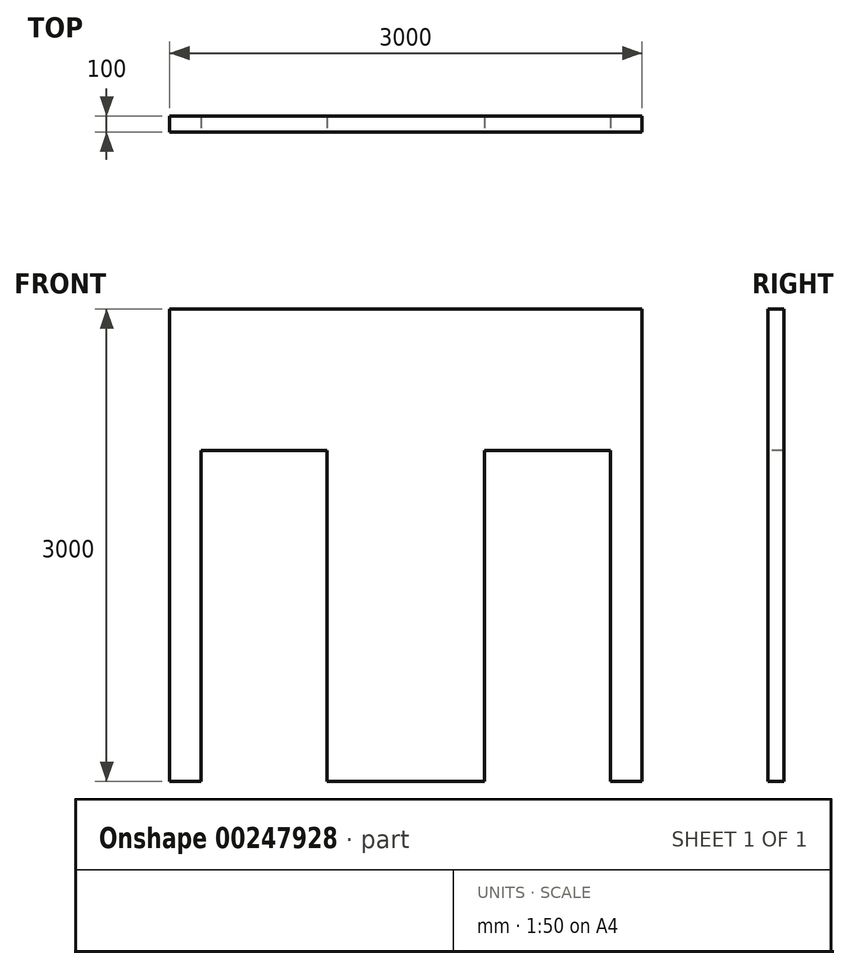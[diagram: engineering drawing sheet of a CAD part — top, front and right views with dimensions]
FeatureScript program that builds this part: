
annotation { "Feature Type Name" : "Feature", "Feature Type Description" : "" }
export const myFeature = defineFeature(function(context is Context, id is Id, definition is map)
    precondition{}
    {
        {
            var Q0;
            Q0=qCreatedBy(makeId("Front.planeOp"),FACE);
            var sketch = newSketch(context, id + "F0", { "sketchPlane" : qUnion([Q0])});
            skLineSegment(sketch, "E0.bottom", {"start": v(1500, 0) * mm, "end": v(-1500, 0) * mm});
            skLineSegment(sketch, "E0.top", {"start": v(1500, 3000) * mm, "end": v(-1500, 3000) * mm});
            skLineSegment(sketch, "E0.left", {"start": v(1500, 0) * mm, "end": v(1500, 3000) * mm});
            skLineSegment(sketch, "E0.right", {"start": v(-1500, 0) * mm, "end": v(-1500, 3000) * mm});
            skPoint(sketch, "E0.middle", {"position": v(0, 1500) * mm});
            skSolve(sketch);
        }
        {
            var Q0;
            Q0=makeQuery(id+"F0.imprint","IMPRINT",FACE,{"disambiguationData":[TD([[makeQuery(id+"F0.imprint","IMPRINT",EDGE,{"derivedFrom":sQuery(id+"F0.wireOp",EDGE,"E0.bottom")}),-1.0]])]});
            extrude(context, id + "F1", {"entities" : qUnion([Q0]), "endBound" : BoundingType.SYMMETRIC, "depth" : 100 * mm});
        }
        {
            var Q0;
            Q0=makeQuery(id+"F1.opExtrude","CAP_FACE",FACE,{"disambiguationData":[OSD([sQuery(id+"F0.wireOp",EDGE,"E0.bottom"),sQuery(id+"F0.wireOp",EDGE,"E0.top"),sQuery(id+"F0.wireOp",EDGE,"E0.left"),sQuery(id+"F0.wireOp",EDGE,"E0.right")])],"isStart":false});
            var sketch = newSketch(context, id + "F2", { "sketchPlane" : qUnion([Q0])});
            skLineSegment(sketch, "E1.bottom", {"start": v(1300, 0) * mm, "end": v(500, 0) * mm});
            skLineSegment(sketch, "E1.top", {"start": v(1300, 2100) * mm, "end": v(500, 2100) * mm});
            skLineSegment(sketch, "E1.left", {"start": v(1300, 0) * mm, "end": v(1300, 2100) * mm});
            skLineSegment(sketch, "E1.right", {"start": v(500, 0) * mm, "end": v(500, 2100) * mm});
            skPoint(sketch, "E1.middle", {"position": v(900, 1050) * mm});
            skLineSegment(sketch, "E2", {"start": v(-1500, 3000) * mm, "end": v(500, 3000) * mm, "construction": true});
            skLineSegment(sketch, "E3", {"start": v(0, 3000) * mm, "end": v(0, 0) * mm, "construction": true});
            skPoint(sketch, "E4.MirrorP", {"position": v(-900, 1050) * mm});
            skLineSegment(sketch, "E5.MirrorCS", {"start": v(-1300, 2100) * mm, "end": v(-500, 2100) * mm});
            skLineSegment(sketch, "E6.MirrorCS", {"start": v(-500, 0) * mm, "end": v(-500, 2100) * mm});
            skLineSegment(sketch, "E7.MirrorCS", {"start": v(-1300, 0) * mm, "end": v(-1300, 2100) * mm});
            skLineSegment(sketch, "E8.MirrorCS", {"start": v(-1300, 0) * mm, "end": v(-500, 0) * mm});
            skSolve(sketch);
        }
        {
            var Q0;
            Q0=makeQuery(id+"F2.imprint","IMPRINT",FACE,{"disambiguationData":[TD([[makeQuery(id+"F2.imprint","IMPRINT",EDGE,{"derivedFrom":sQuery(id+"F2.wireOp",EDGE,"E1.bottom")}),-1.0]])]});
            var Q1;
            Q1=makeQuery(id+"F2.imprint","IMPRINT",FACE,{"disambiguationData":[TD([[makeQuery(id+"F2.imprint","IMPRINT",EDGE,{"derivedFrom":sQuery(id+"F2.wireOp",EDGE,"E5.MirrorCS")}),-1.0]])]});
            extrude(context, id + "F3", {"entities" : qUnion([Q0, Q1]), "operationType" : NewBodyOperationType.REMOVE, "endBound" : BoundingType.THROUGH_ALL, "oppositeDirection" : true, "depth" : 25 * mm});
        }
    });
